# Revit family: cav-mp1180_2360vb-n_60Hz
name_source: partatom
category: 機械設備
units: mm (PartAtom-declared; Revit-internal decimal feet)

## family parameters
OmniClass タイトル = Packaged Water Chillers
OmniClass 番号 = 23.75.10.24.21.21
パーツ タイプ = 標準
ロード時にボイドで切り取り = いいえ
丸型コネクタ寸法 = 直径を使用
作業面ベース = いいえ
共有 = いいえ
常に垂直 = はい
部屋計算ポイント = いいえ

## types (5) — shared parameters
Clearance Back = 900  [stored 2.95276 ft]
Clearance Front = 900  [stored 2.95276 ft]
Clearance Right = 900  [stored 2.95276 ft]
Clearance Top = 1000  [stored 3.28084 ft]
Depth = 3400  [stored 11.1549 ft]
Height = 2350
IfcExportAs = IfcChillerType
IfcExportType = AIRCOOLED
OmniClassCode = 23-33 21 13 13 11
S2寸法 = 162  [stored 0.531496 ft]
S寸法 = 150  [stored 0.492126 ft]
URL = https://www.mitsubishielectric.co.jp
Uniclass2015Code = Pr_60_60_13_04
Uniclass2015Title = Air cooled liquid chillers
Uniclass2015Version = Systems v1.9
Width = 1080  [stored 3.54331 ft]
ドレン管径 = 49
ユニット間隔 = 50  [stored 0.164042 ft]
仕様書バージョン = Version1.0
企業コード = 108420
冷水入口温度_一次側 = 12 °C
冷水出口温度_一次側 = 7 °C
冷水管径 = 76
分類コード = 50051002500020
参照している仕様書等のバージョン = 公共建築工事標準仕様書（機械設備工事編）平成31年度版
周波数 = 60 Hz
呼称 = 空冷モジュールチラー
始動方式 = INV
損失水頭_温水一次側 = 0.0 Pa
極数 = 3
法定耐用年数 = 15
温水入口温度_一次側 = 0 °C
温水出口温度_一次側 = 0 °C
相 = 3
相_補機 = 1
積算_科目 = 1 空気調和設備
符号 = RR
製品出荷対象 = 国内
製造元 = 三菱電機株式会社
設置方法 = 床置形
説明 = 空冷式ヒートポンプチラー
負荷分類 = 1_熱源類
電圧 = 400 V
電圧_補機 = 0 V
zero-valued in all types: 価格, 機械基礎_D, 機械基礎_H, 耐震強度

## per-type parameters (varying)
| type | Clearance Left | モデル | 損失水頭_冷水一次側 | 製品リリース年月 |
| cav-mp1180vb-n | 900  [stored 2.95276 ft] | CAV-MP1180VB-N | 36000.0 Pa | 2020/4/27 |
| cav-mp1500vb-n | 900  [stored 2.95276 ft] | CAV-MP1500VB-N | 56000.0 Pa | 2020/4/27 |
| cav-mp1800vb-n | 900  [stored 2.95276 ft] | CAV-MP1800VB-N | 79000.0 Pa | 2020/4/27 |
| cav-mp2000vb-n | 1200  [stored 3.93701 ft] | CAV-MP2000VB-N | 96000.0 Pa | 2020/4/27 |
| cav-mp2360vb-n | 1200  [stored 3.93701 ft] | CAV-MP2360VB-N | 131000.0 Pa | 2021/7/15 |

note: [stored X ft] marks values corroborated as IEEE doubles in the binary element streams (Revit-internal decimal feet)
